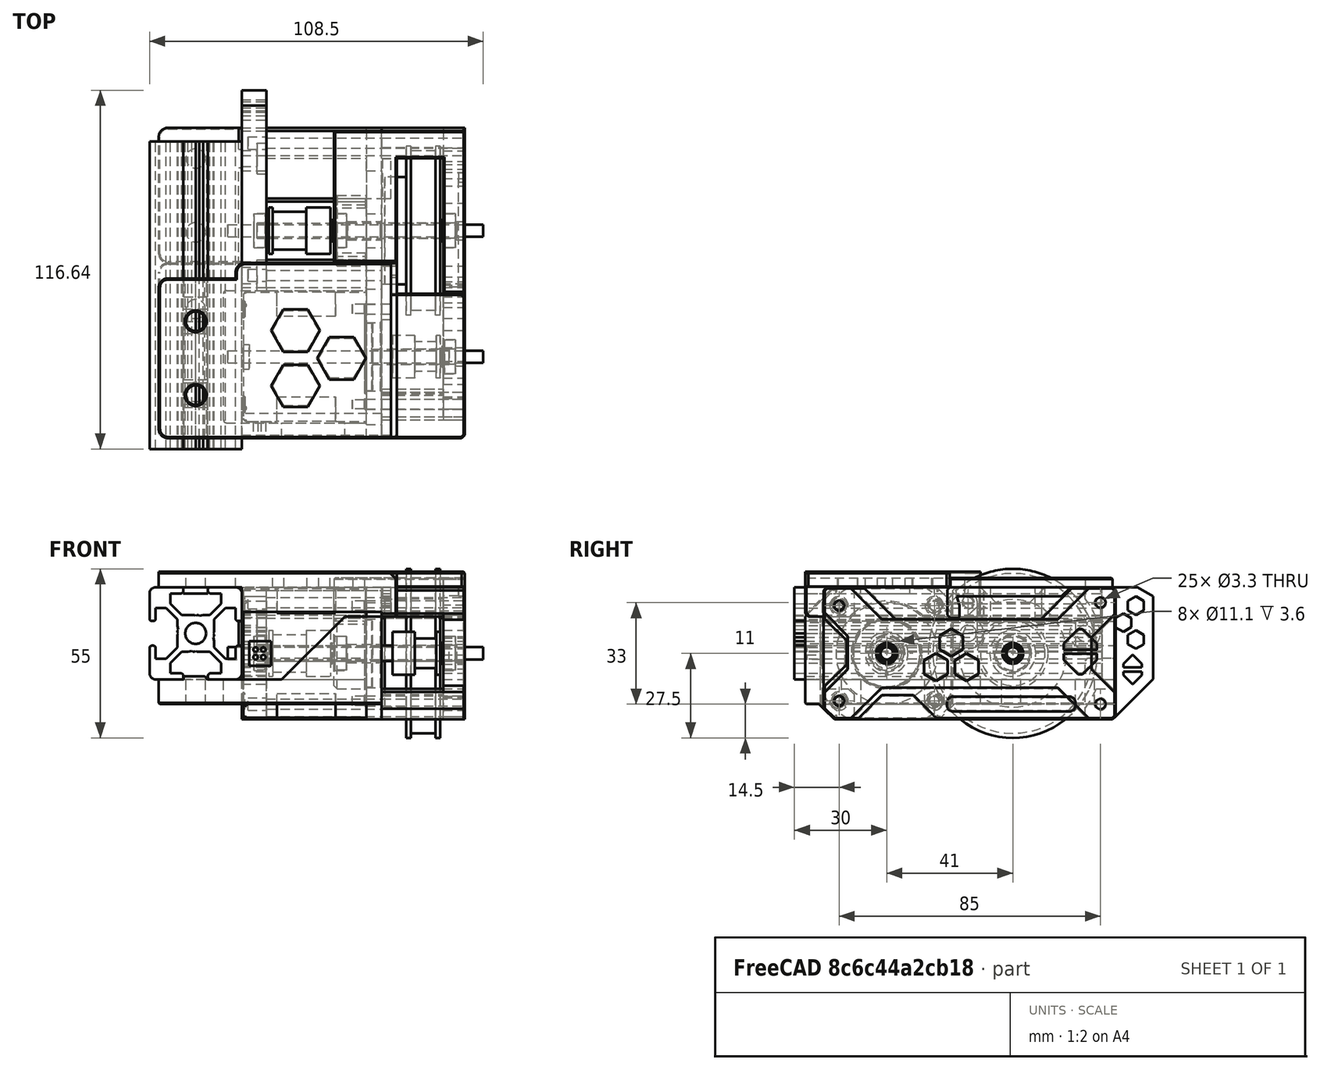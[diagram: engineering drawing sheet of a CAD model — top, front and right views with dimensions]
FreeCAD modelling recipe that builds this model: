
FCSTD DOCUMENT  (FreeCAD 0.19R24291 (Git))
Label: 80t-gearbox-old
License: Other
LicenseURL: GPL3
objects: Part::Cylinder×41, Part::Box×39, Part::Chamfer×38, Part::Cut×30, Part::MultiFuse×30, Part::Feature×29, Part::Fillet×4, Part::Refine×3
note: 214 computed .brp shape members not serialized (recipe doc carries the construction recipe); baked Part::Feature solids carry a one-line shape summary decoded from their .brp

FEATURE [Part::Feature] Cut001002  label="80t-pulley"
  Placement = pos=(64.5,41,8.5) rot=(0.707107,0,-0.707107;3.14159rad)
  shape: bbox 18 x 55 x 55 mm, 10 faces (baked)
FEATURE [Part::Feature] Cut001001  label="16t-pulley"
  Placement = pos=(64.5,0,8.5) rot=(0,-1,0;1.5708rad)
  shape: bbox 15.5 x 13.9 x 13.9 mm, 8 faces (baked)
FEATURE [Part::Feature] Fusion006002011004053036004001001  label="motor-40mm"
  Placement = pos=(0.5,0,8.5) rot=(0,1,0;1.5708rad)
  shape: bbox 67 x 47 x 42 mm, 100 faces (baked)
FEATURE [Part::Feature] Extrude001003002002002002  label="Extrude001003002002004"
  Placement = pos=(-15,-30,15) rot=(-1,0,0;1.5708rad)
  shape: bbox 30 x 100 x 30 mm, 95 faces (baked)
FEATURE [Part::Feature] Cut001  label="20t-pulley"
  Placement = pos=(8.8,41,8.5) rot=(0.707107,0,0.707107;3.14159rad)
  shape: bbox 20 x 15 x 15 mm, 8 faces (baked)
FEATURE [Part::Feature] Cut001003  label="MR115ZZ001"
  Placement = pos=(69.5,0,8.5) rot=(0,-1,0;1.5708rad)
  shape: bbox 4 x 11 x 11 mm, 4 faces (baked)
FEATURE [Part::Feature] Cut001004  label="MR115ZZ002"
  Placement = pos=(69.5,41,8.5) rot=(0,-1,0;1.5708rad)
  shape: bbox 4 x 11 x 11 mm, 4 faces (baked)
FEATURE [Part::Feature] Cut001005  label="MR115ZZ003"
  Placement = pos=(34,41,8.5) rot=(0,-1,0;1.5708rad)
  shape: bbox 4 x 11 x 11 mm, 4 faces (baked)
FEATURE [Part::Cylinder] Cylinder  label="POSA"
  Angle = 360
  AttacherType = Attacher::AttachEngine3D
  Height = 83
  Placement = pos=(-4.5,0,8.5) rot=(0,1,0;1.5708rad)
  Radius = 2
FEATURE [Part::Cylinder] Cylinder001  label="POSB"
  Angle = 360
  AttacherType = Attacher::AttachEngine3D
  Height = 83
  Placement = pos=(-4.5,41,8.5) rot=(0,1,0;1.5708rad)
  Radius = 2
FEATURE [Part::Box] Box  label="Cube"
  AttacherType = Attacher::AttachEngine3D
  Height = 43
  Length = 5
  Placement = pos=(40.5,-26.5,-13) rot=(0,0,1;0rad)
  Width = 101
FEATURE [Part::Box] Box001  label="Cube001"
  AttacherType = Attacher::AttachEngine3D
  Height = 43
  Length = 8
  Placement = pos=(0,21.5,-13) rot=(0,0,1;0rad)
  Width = 53
FEATURE [Part::Cylinder] Cylinder002  label="br01"
  Angle = 360
  AttacherType = Attacher::AttachEngine3D
  Height = 4
  Placement = pos=(4,41,8.5) rot=(0,1,0;1.5708rad)
  Radius = 5.55
FEATURE [Part::Cylinder] Cylinder003  label="br002"
  Angle = 360
  AttacherType = Attacher::AttachEngine3D
  Height = 4
  Placement = pos=(30,41,8.5) rot=(0,1,0;1.5708rad)
  Radius = 5.55
FEATURE [Part::Cylinder] Cylinder004  label="br003"
  Angle = 360
  AttacherType = Attacher::AttachEngine3D
  Height = 4
  Placement = pos=(65.5,41,8.5) rot=(0,1,0;1.5708rad)
  Radius = 5.55
FEATURE [Part::Cylinder] Cylinder005  label="br004"
  Angle = 360
  AttacherType = Attacher::AttachEngine3D
  Height = 4
  Placement = pos=(65.5,0,8.5) rot=(0,1,0;1.5708rad)
  Radius = 5.55
FEATURE [Part::Box] Box002  label="Cube002"
  AttacherType = Attacher::AttachEngine3D
  Height = 8
  Length = 27
  Placement = pos=(-27,30.5,-8) rot=(0,0,1;0rad)
  Width = 44
FEATURE [Part::Box] Box003  label="Cube003"
  AttacherType = Attacher::AttachEngine3D
  Height = 7.8
  Length = 1
  Placement = pos=(-1,29.5,11.1) rot=(0,0,1;0rad)
  Width = 32
FEATURE [Part::Feature] Cut001006  label="MR115ZZ004"
  Placement = pos=(8,41,8.5) rot=(0,-1,0;1.5708rad)
  shape: bbox 4 x 11 x 11 mm, 4 faces (baked)
FEATURE [Part::Cut] Cut
  Base = -> Box001
  Tool = -> Cylinder002
FEATURE [Part::Chamfer] Chamfer
  Base = -> Cut
  Edges = 1 edges r=0.4: [Edge13]
FEATURE [Part::Cylinder] Cylinder006  label="Cylinder"
  Angle = 360
  AttacherType = Attacher::AttachEngine3D
  Height = 10
  Placement = pos=(-3e-15,26.5,15) rot=(0,1,0;1.5708rad)
  Radius = 2.65
FEATURE [Part::Cylinder] Cylinder007  label="Cylinder001"
  Angle = 360
  AttacherType = Attacher::AttachEngine3D
  Height = 3
  Placement = pos=(5,26.5,15) rot=(0,1,0;1.5708rad)
  Radius = 5
FEATURE [Part::MultiFuse] Fusion
  Shapes = -> [Cylinder007,Cylinder006]
FEATURE [Part::Feature] Fusion006002011004053036004001002  label="Fusion001"
  Placement = pos=(0,38,0) rot=(0,0,1;0rad)
  shape: bbox 10 x 10 x 10 mm, 7 faces (baked)
FEATURE [Part::MultiFuse] Fusion006002011004053036004001003
  Shapes = -> [Fusion,Fusion006002011004053036004001002]
FEATURE [Part::Box] Box004  label="Cube004"
  AttacherType = Attacher::AttachEngine3D
  Height = 10
  Length = 3
  Placement = pos=(5,16.5,10) rot=(0,0,1;0rad)
  Width = 10
FEATURE [Part::MultiFuse] Fusion006002011004053036004001004
  Shapes = -> [Box004,Fusion006002011004053036004001003]
FEATURE [Part::Cut] Cut001007
  Base = -> Chamfer
  Tool = -> Fusion006002011004053036004001004
FEATURE [Part::Box] Box005  label="Cube005"
  AttacherType = Attacher::AttachEngine3D
  Height = 7.8
  Length = 1
  Placement = pos=(-1,67.5,11.1) rot=(0,0,1;0rad)
  Width = 7
FEATURE [Part::Box] Box006  label="Cube006"
  AttacherType = Attacher::AttachEngine3D
  Height = 13
  Length = 10
  Placement = pos=(-1.5,20.5,-13) rot=(0,0,1;0rad)
  Width = 10
FEATURE [Part::Cut] Cut001008
  Base = -> Cut001007
  Tool = -> Box006
FEATURE [Part::Chamfer] Chamfer001
  Base = -> Cut001008
  Edges = 1 edges r=5: [Edge30]
FEATURE [Part::Fillet] Fillet
  Base = -> Box002
  Edges = 2 edges r=3: [Edge1,Edge3]
FEATURE [Part::Box] Box007  label="Cube007"
  AttacherType = Attacher::AttachEngine3D
  Height = 28.5
  Length = 28
  Placement = pos=(13,-26.5,-8) rot=(0,0,1;0rad)
  Width = 5
FEATURE [Part::Box] Box009  label="Cube009"
  AttacherType = Attacher::AttachEngine3D
  Height = 8
  Length = 72
  Placement = pos=(-27,-26.5,-8) rot=(0,0,1;0rad)
  Width = 57
FEATURE [Part::Box] Box010  label="Cube010"
  AttacherType = Attacher::AttachEngine3D
  Height = 8
  Length = 40.5
  Placement = pos=(0,-21.5,-8) rot=(0,0,1;0rad)
  Width = 43
FEATURE [Part::Fillet] Fillet001
  Base = -> Box009
  Edges = 2 edges r=3: [Edge1,Edge3]
FEATURE [Part::Cut] Cut001009
  Base = -> Fillet001
  Tool = -> Box010
FEATURE [Part::Box] Box011  label="Cube011"
  AttacherType = Attacher::AttachEngine3D
  Height = 10
  Length = 33
  Placement = pos=(8,50.5,20) rot=(0,0,1;0rad)
  Width = 24
FEATURE [Part::Box] Box012  label="Cube012"
  AttacherType = Attacher::AttachEngine3D
  Height = 20
  Length = 33
  Placement = pos=(8,64.5,-13) rot=(0,0,1;0rad)
  Width = 10
FEATURE [Part::Box] Box013  label="Cube013"
  AttacherType = Attacher::AttachEngine3D
  Height = 10
  Length = 33
  Placement = pos=(8,21.5,20) rot=(0,0,1;0rad)
  Width = 10
FEATURE [Part::Chamfer] Chamfer002
  Base = -> Chamfer001
  Edges = 4 edges r=1: [Edge16,Edge19,Edge24,Edge25]
FEATURE [Part::Chamfer] Chamfer005
  Base = -> Box013
  Edges = 4 edges r=1: [Edge9,Edge10,Edge11,Edge12]
FEATURE [Part::Chamfer] Chamfer006
  Base = -> Chamfer002
  Edges = 2 edges r=1: [Edge39,Edge43]
FEATURE [Part::Box] Box014  label="Cube014"
  AttacherType = Attacher::AttachEngine3D
  Height = 10
  Length = 10
  Placement = pos=(-1,30.5,-18) rot=(0,0,1;0rad)
  Width = 35
FEATURE [Part::Chamfer] Chamfer007
  Base = -> Box014
  Edges = 1 edges r=5: [Edge12]
FEATURE [Part::Cut] Cut001010
  Base = -> Chamfer006
  Tool = -> Chamfer007
FEATURE [Part::Cylinder] Cylinder008  label="Cylinder002"
  Angle = 360
  AttacherType = Attacher::AttachEngine3D
  Height = 110
  Placement = pos=(2,26.5,25) rot=(0,1,0;1.5708rad)
  Radius = 1.65
FEATURE [Part::Cylinder] Cylinder009  label="Cylinder003"
  Angle = 360
  AttacherType = Attacher::AttachEngine3D
  Height = 110
  Placement = pos=(2,69.5,25) rot=(0,1,0;1.5708rad)
  Radius = 1.65
FEATURE [Part::Cylinder] Cylinder010  label="Cylinder004"
  Angle = 360
  AttacherType = Attacher::AttachEngine3D
  Height = 110
  Placement = pos=(2,69.5,-8) rot=(0,1,0;1.5708rad)
  Radius = 1.65
FEATURE [Part::Cylinder] Cylinder011  label="Cylinder005"
  Angle = 360
  AttacherType = Attacher::AttachEngine3D
  Height = 6
  Placement = pos=(2,69.5,-8) rot=(0,1,0;1.5708rad)
  Radius = 2
FEATURE [Part::Cylinder] Cylinder012  label="Cylinder006"
  Angle = 360
  AttacherType = Attacher::AttachEngine3D
  Height = 6
  Placement = pos=(2,69.5,25) rot=(0,1,0;1.5708rad)
  Radius = 2
FEATURE [Part::Cylinder] Cylinder013  label="Cylinder007"
  Angle = 360
  AttacherType = Attacher::AttachEngine3D
  Height = 6
  Placement = pos=(2,26.5,25) rot=(0,1,0;1.5708rad)
  Radius = 2
FEATURE [Part::MultiFuse] Fusion006002011004053036004001006
  Shapes = -> [Cylinder013,Cylinder012,Cylinder011]
FEATURE [Part::Cut] Cut001011
  Base = -> Cut001010
  Tool = -> Fusion006002011004053036004001006
FEATURE [Part::MultiFuse] Fusion006002011004053036004001007
  Shapes = -> [Cylinder010,Cylinder008,Cylinder009]
FEATURE [Part::Chamfer] Chamfer008
  Base = -> Box
  Edges = 2 edges r=1: [Edge11,Edge12]
FEATURE [Part::Chamfer] Chamfer009
  Base = -> Box011
  Edges = 4 edges r=1: [Edge9,Edge10,Edge11,Edge12]
FEATURE [Part::Cylinder] Cylinder014  label="Cylinder008"
  Angle = 360
  AttacherType = Attacher::AttachEngine3D
  Height = 10
  Placement = pos=(-15,40.5,0) rot=(0,0,1;0rad)
  Radius = 3.15
FEATURE [Part::Cylinder] Cylinder015  label="Cylinder009"
  Angle = 360
  AttacherType = Attacher::AttachEngine3D
  Height = 10
  Placement = pos=(-15,64.5,0) rot=(0,0,1;0rad)
  Radius = 3.15
FEATURE [Part::MultiFuse] Fusion006002011004053036004001009
  Placement = pos=(0,0,-10) rot=(0,0,1;0rad)
  Shapes = -> [Cylinder014,Cylinder015]
FEATURE [Part::Cut] Cut001012
  Base = -> Fillet
  Tool = -> Fusion006002011004053036004001009
FEATURE [Part::Chamfer] Chamfer011
  Base = -> Cut001012
  Edges = 5 edges r=0.4: [Edge4,Edge12,Edge14,Edge16,Edge17]
FEATURE [Part::Chamfer] Chamfer012
  Base = -> Cut001011
  Edges = 1 edges r=0.4: [Edge45]
FEATURE [Part::MultiFuse] Fusion006002011004053036004001010
  Shapes = -> [Box005,Box003]
FEATURE [Part::MultiFuse] Fusion006002011004053036004001011  label="back-plate"
  Shapes = -> [Chamfer012,Fusion006002011004053036004001010,Chamfer011]
FEATURE [Part::Box] Box015  label="Cube015"
  AttacherType = Attacher::AttachEngine3D
  Height = 10
  Length = 10
  Placement = pos=(36.5,17,-18) rot=(0,0,1;0rad)
  Width = 48.5
FEATURE [Part::Box] Box016  label="Cube016"
  AttacherType = Attacher::AttachEngine3D
  Height = 10
  Length = 10
  Placement = pos=(36.5,-75.5,-18) rot=(0,0,1;0rad)
  Width = 58.5
FEATURE [Part::Chamfer] Chamfer013
  Base = -> Box016
  Edges = 1 edges r=5: [Edge12]
FEATURE [Part::Cut] Cut001013
  Base = -> Chamfer008
  Tool = -> Chamfer013
FEATURE [Part::Chamfer] Chamfer014
  Base = -> Box015
  Edges = 2 edges r=5: [Edge10,Edge12]
FEATURE [Part::Cut] Cut001014
  Base = -> Cut001013
  Tool = -> Chamfer014
FEATURE [Part::Chamfer] Chamfer015
  Base = -> Cut001014
  Edges = 1 edges r=9.5: [Edge33]
FEATURE [Part::Chamfer] Chamfer016
  Base = -> Cut001009
  Edges = 5 edges r=0.4: [Edge4,Edge14,Edge16,Edge18,Edge19]
FEATURE [Part::Cylinder] Cylinder016  label="POSA001"
  Angle = 360
  AttacherType = Attacher::AttachEngine3D
  Height = 83
  Placement = pos=(2.5,0,8.5) rot=(0,1,0;1.5708rad)
  Radius = 11.15
FEATURE [Part::Chamfer] Chamfer017
  Base = -> Chamfer015
  Edges = 1 edges r=0.4: [Edge16]
FEATURE [Part::Cylinder] Cylinder017  label="Cylinder010"
  Angle = 360
  AttacherType = Attacher::AttachEngine3D
  Height = 10
  Placement = pos=(-15,15.5,0) rot=(0,0,1;0rad)
  Radius = 3.15
FEATURE [Part::Cylinder] Cylinder018  label="Cylinder011"
  Angle = 360
  AttacherType = Attacher::AttachEngine3D
  Height = 10
  Placement = pos=(-15,-11.5,0) rot=(0,0,1;0rad)
  Radius = 3.15
FEATURE [Part::MultiFuse] Fusion006002011004053036004001012
  Placement = pos=(0,0,-9) rot=(0,0,1;0rad)
  Shapes = -> [Cylinder017,Cylinder018]
FEATURE [Part::Cut] Cut001015
  Base = -> Chamfer016
  Tool = -> Fusion006002011004053036004001012
FEATURE [Part::Chamfer] Chamfer018
  Base = -> Box007
  Edges = 1 edges r=0.5: [Edge9]
FEATURE [Part::Chamfer] Chamfer019
  Base = -> Chamfer018
  Edges = 1 edges r=20.5: [Edge3]
FEATURE [Part::Box] Box017  label="Cube017"
  AttacherType = Attacher::AttachEngine3D
  Height = 2
  Length = 7.8
  Placement = pos=(-18.9,-26.5,0) rot=(0,0,1;0rad)
  Width = 11
FEATURE [Part::Box] Box018  label="Cube018"
  AttacherType = Attacher::AttachEngine3D
  Height = 2
  Length = 7.8
  Placement = pos=(-18.9,-7.5,0) rot=(0,0,1;0rad)
  Width = 19
FEATURE [Part::Box] Box019  label="Cube019"
  AttacherType = Attacher::AttachEngine3D
  Height = 2
  Length = 7.8
  Placement = pos=(-18.9,19.5,0) rot=(0,0,1;0rad)
  Width = 11
FEATURE [Part::MultiFuse] Fusion006002011004053036004001013
  Placement = pos=(0,0,-1) rot=(0,0,1;0rad)
  Shapes = -> [Box018,Box019,Box017]
FEATURE [Part::Chamfer] Chamfer020
  Base = -> Fusion006002011004053036004001013
  Edges = 3 edges r=1: [Edge6,Edge18,Edge30]
FEATURE [Part::MultiFuse] Fusion006002011004053036004001014
  Shapes = -> [Chamfer020,Cut001015]
FEATURE [Part::MultiFuse] Fusion006002011004053036004001015
  Shapes = -> [Fusion006002011004053036004001014,Chamfer019,Chamfer017]
FEATURE [Part::Cut] Cut001016
  Base = -> Fusion006002011004053036004001015
  Tool = -> Cylinder016
FEATURE [Part::Cylinder] Cylinder019  label="POSA002"
  Angle = 360
  AttacherType = Attacher::AttachEngine3D
  Height = 30
  Placement = pos=(32,15.5,24) rot=(0,1,0;1.5708rad)
  Radius = 1.65
FEATURE [Part::Cylinder] Cylinder020  label="POSA003"
  Angle = 360
  AttacherType = Attacher::AttachEngine3D
  Height = 30
  Placement = pos=(32,-15.5,24) rot=(0,1,0;1.5708rad)
  Radius = 1.65
FEATURE [Part::Cylinder] Cylinder021  label="POSA004"
  Angle = 360
  AttacherType = Attacher::AttachEngine3D
  Height = 30
  Placement = pos=(32,-15.5,-7) rot=(0,1,0;1.5708rad)
  Radius = 1.65
FEATURE [Part::Cylinder] Cylinder022  label="POSA005"
  Angle = 360
  AttacherType = Attacher::AttachEngine3D
  Height = 30
  Placement = pos=(32,15.5,-7) rot=(0,1,0;1.5708rad)
  Radius = 1.65
FEATURE [Part::MultiFuse] Fusion006002011004053036004001016
  Shapes = -> [Cylinder022,Cylinder021,Cylinder020,Cylinder019]
FEATURE [Part::Cut] Cut001017
  Base = -> Cut001016
  Tool = -> Fusion006002011004053036004001016
FEATURE [Part::Cylinder] Cylinder023  label="POSB001"
  Angle = 360
  AttacherType = Attacher::AttachEngine3D
  Height = 12
  Placement = pos=(30,41,8.5) rot=(0,1,0;1.5708rad)
  Radius = 11.5
FEATURE [Part::Chamfer] Chamfer021
  Base = -> Cylinder023
  Edges = 1 edges r=1: [Edge3]
FEATURE [Part::Cut] Cut001018
  Base = -> Chamfer021
  Tool = -> Cylinder003
FEATURE [Part::Chamfer] Chamfer022
  Base = -> Cut001018
  Edges = 1 edges r=0.4: [Edge6]
FEATURE [Part::Cylinder] Cylinder024  label="POSB002"
  Angle = 360
  AttacherType = Attacher::AttachEngine3D
  Height = 83
  Placement = pos=(-4.5,41,8.5) rot=(0,1,0;1.5708rad)
  Radius = 3
FEATURE [Part::Chamfer] Chamfer023
  Base = -> Box012
  Edges = 4 edges r=1: [Edge9,Edge10,Edge11,Edge12]
FEATURE [Part::MultiFuse] Fusion006002011004053036004001017
  Shapes = -> [Chamfer023,Chamfer009,Chamfer005]
FEATURE [Part::MultiFuse] Fusion006002011004053036004001018
  Shapes = -> [Cut001017,Chamfer022]
FEATURE [Part::Cut] Cut001019
  Base = -> Fusion006002011004053036004001018
  Tool = -> Cylinder024
FEATURE [Part::Chamfer] Chamfer024
  Base = -> Cut001019
  Edges = 3 edges r=0.4: [Edge126,Edge173,Edge202]
FEATURE [Part::MultiFuse] Fusion006002011004053036004001019
  Shapes = -> [Chamfer024,Fusion006002011004053036004001017]
FEATURE [Part::Box] Box020  label="Cube020"
  AttacherType = Attacher::AttachEngine3D
  Height = 10
  Length = 10
  Placement = pos=(38.5,30.5,35) rot=(0,0,1;0rad)
  Width = 21
FEATURE [Part::Chamfer] Chamfer025
  Base = -> Box020
  Edges = 2 edges r=5: [Edge9,Edge11]
  Placement = pos=(0,0,-10) rot=(0,0,1;0rad)
FEATURE [Part::Cut] Cut001020
  Base = -> Fusion006002011004053036004001019
  Tool = -> Fusion006002011004053036004001007
FEATURE [Part::Cut] Cut001021  label="z-motor-plate"
  Base = -> Cut001020
  Tool = -> Chamfer025
FEATURE [Part::Box] Box021  label="Cube021"
  AttacherType = Attacher::AttachEngine3D
  Height = 10
  Length = 5
  Placement = pos=(45.5,-26.5,20.5) rot=(0,0,1;0rad)
  Width = 57
FEATURE [Part::Box] Box022  label="Cube022"
  AttacherType = Attacher::AttachEngine3D
  Height = 9
  Length = 50.5
  Placement = pos=(0,-26.5,22) rot=(0,0,1;0rad)
  Width = 8
FEATURE [Part::Chamfer] Chamfer026
  Base = -> Box022
  Edges = 1 edges r=7: [Edge11]
FEATURE [Part::Box] Box023  label="Cube023"
  AttacherType = Attacher::AttachEngine3D
  Height = 5
  Length = 77.5
  Placement = pos=(-27,-26.5,30) rot=(0,0,1;0rad)
  Width = 57
FEATURE [Part::Chamfer] Chamfer027
  Base = -> Box021
  Edges = 2 edges r=1: [Edge9,Edge11]
FEATURE [Part::Cylinder] Cylinder025  label="POSA006"
  Angle = 360
  AttacherType = Attacher::AttachEngine3D
  Height = 83
  Placement = pos=(18.5,0,8.5) rot=(0,1,0;1.5708rad)
  Radius = 17
FEATURE [Part::Cut] Cut001022
  Base = -> Chamfer027
  Tool = -> Cylinder025
FEATURE [Part::Box] Box024  label="Cube024"
  AttacherType = Attacher::AttachEngine3D
  Height = 2
  Length = 8
  Placement = pos=(-19,-8.5,28) rot=(0,0,1;0rad)
  Width = 16
FEATURE [Part::Box] Box025  label="Cube025"
  AttacherType = Attacher::AttachEngine3D
  Height = 2
  Length = 8
  Placement = pos=(-19,-26.5,28) rot=(0,0,1;0rad)
  Width = 10
FEATURE [Part::Box] Box026  label="Cube026"
  AttacherType = Attacher::AttachEngine3D
  Height = 2
  Length = 8
  Placement = pos=(-19,15.5,28) rot=(0,0,1;0rad)
  Width = 10
FEATURE [Part::Cylinder] Cylinder026  label="Cylinder012"
  Angle = 360
  AttacherType = Attacher::AttachEngine3D
  Height = 10
  Placement = pos=(-15,11.5,26) rot=(0,0,1;0rad)
  Radius = 3.15
FEATURE [Part::Cylinder] Cylinder027  label="Cylinder013"
  Angle = 360
  AttacherType = Attacher::AttachEngine3D
  Height = 10
  Placement = pos=(-15,-12.5,26) rot=(0,0,1;0rad)
  Radius = 3.15
FEATURE [Part::Cylinder] Cylinder028  label="POSA007"
  Angle = 360
  AttacherType = Attacher::AttachEngine3D
  Height = 83
  Placement = pos=(25.5,-15.5,24) rot=(0,1,0;1.5708rad)
  Radius = 1.65
FEATURE [Part::Cylinder] Cylinder029  label="POSA008"
  Angle = 360
  AttacherType = Attacher::AttachEngine3D
  Height = 83
  Placement = pos=(25.5,15.5,24) rot=(0,1,0;1.5708rad)
  Radius = 1.65
FEATURE [Part::MultiFuse] Fusion006002011004053036004001024
  Shapes = -> [Cylinder029,Cylinder028]
FEATURE [Part::Box] Box027  label="Cube027"
  AttacherType = Attacher::AttachEngine3D
  Height = 10
  Length = 26
  Placement = pos=(45.5,64.5,-13) rot=(0,0,1;0rad)
  Width = 10
FEATURE [Part::Box] Box028  label="Cube028"
  AttacherType = Attacher::AttachEngine3D
  Height = 10
  Length = 26
  Placement = pos=(45.5,64.5,20) rot=(0,0,1;0rad)
  Width = 10
FEATURE [Part::Box] Box029  label="Cube029"
  AttacherType = Attacher::AttachEngine3D
  Height = 9.5
  Length = 21
  Placement = pos=(50.5,-20.5,20.5) rot=(0,0,1;0rad)
  Width = 10
FEATURE [Part::Box] Box030  label="Cube030"
  AttacherType = Attacher::AttachEngine3D
  Height = 10
  Length = 26
  Placement = pos=(45.5,-20.5,-13) rot=(0,0,1;0rad)
  Width = 10
FEATURE [Part::Cylinder] Cylinder030  label="POSB003"
  Angle = 360
  AttacherType = Attacher::AttachEngine3D
  Height = 83
  Placement = pos=(20.5,41,8.5) rot=(0,1,0;1.5708rad)
  Radius = 29.5
FEATURE [Part::Cylinder] Cylinder031  label="POSA009"
  Angle = 360
  AttacherType = Attacher::AttachEngine3D
  Height = 83
  Placement = pos=(-4.5,0,8.5) rot=(0,1,0;1.5708rad)
  Radius = 17
FEATURE [Part::MultiFuse] Fusion006002011004053036004001025
  Shapes = -> [Box030,Box029,Box027,Box028]
FEATURE [Part::Cut] Cut001024002
  Base = -> Fusion006002011004053036004001025
  Tool = -> Cylinder030
FEATURE [Part::Chamfer] Chamfer030
  Base = -> Cut001024002
  Edges = 1 edges r=3.5: [Edge9]
FEATURE [Part::Cut] Cut001024003
  Base = -> Chamfer030
  Tool = -> Cylinder031
FEATURE [Part::Chamfer] Chamfer031
  Base = -> Cut001024003
  Edges = 11 edges r=1: [Edge9,Edge15,Edge24,Edge26,Edge32,Edge41,Edge44,Edge46,Edge55,Edge57,Edge59]
FEATURE [Part::Box] Box032  label="Cube032"
  AttacherType = Attacher::AttachEngine3D
  Height = 43
  Length = 7
  Placement = pos=(65.5,-20.5,-13) rot=(0,0,1;0rad)
  Width = 95
FEATURE [Part::Chamfer] Chamfer032
  Base = -> Box032
  Edges = 1 edges r=3.5: [Edge9]
FEATURE [Part::Chamfer] Chamfer033
  Base = -> Chamfer032
  Edges = 3 edges r=1: [Edge8,Edge11,Edge13]
FEATURE [Part::Cylinder] Cylinder032  label="POSB004"
  Angle = 360
  AttacherType = Attacher::AttachEngine3D
  Height = 83
  Placement = pos=(-4.5,41,8.5) rot=(0,1,0;1.5708rad)
  Radius = 3
FEATURE [Part::Cylinder] Cylinder033  label="POSA010"
  Angle = 360
  AttacherType = Attacher::AttachEngine3D
  Height = 83
  Placement = pos=(-4.5,0,8.5) rot=(0,1,0;1.5708rad)
  Radius = 3
FEATURE [Part::MultiFuse] Fusion006002011004053036004001026
  Shapes = -> [Cylinder033,Cylinder032,Cylinder005,Cylinder004]
FEATURE [Part::Cut] Cut001024004
  Base = -> Chamfer033
  Tool = -> Fusion006002011004053036004001026
FEATURE [Part::Chamfer] Chamfer034
  Base = -> Cut001024004
  Edges = 4 edges r=0.4: [Edge9,Edge10,Edge31,Edge32]
FEATURE [Part::Feature] Fusion006002011004053036004001028001  label="dog-bone-plate"
  shape: bbox 27 x 95 x 43 mm, 76 faces (baked)
FEATURE [Part::Cylinder] Cylinder034  label="POSB005"
  Angle = 360
  AttacherType = Attacher::AttachEngine3D
  Height = 83
  Placement = pos=(-4.5,69.5,-8) rot=(0,1,0;1.5708rad)
  Radius = 1.65
FEATURE [Part::Cylinder] Cylinder035  label="POSA011"
  Angle = 360
  AttacherType = Attacher::AttachEngine3D
  Height = 83
  Placement = pos=(-4.5,-15.5,-7) rot=(0,1,0;1.5708rad)
  Radius = 1.65
FEATURE [Part::Cylinder] Cylinder036  label="POSB006"
  Angle = 360
  AttacherType = Attacher::AttachEngine3D
  Height = 83
  Placement = pos=(-4.5,69.5,25) rot=(0,1,0;1.5708rad)
  Radius = 1.65
FEATURE [Part::Cylinder] Cylinder037  label="POSA012"
  Angle = 360
  AttacherType = Attacher::AttachEngine3D
  Height = 83
  Placement = pos=(-4.5,-15.5,24) rot=(0,1,0;1.5708rad)
  Radius = 1.65
FEATURE [Part::MultiFuse] Fusion006002011004053036004001028003
  Shapes = -> [Cylinder037,Cylinder036,Cylinder035,Cylinder034]
FEATURE [Part::Cut] Cut001024005  label="dog-bone-plate-r1"
  Base = -> Fusion006002011004053036004001028001
  Tool = -> Fusion006002011004053036004001028003
FEATURE [Part::Feature] Fusion006002011004053036004001028003001  label="Fusion006002011004053036004001028004"
  shape: bbox 83 x 88.3 x 36.3 mm, 12 faces, 4 solids (baked)
FEATURE [Part::MultiFuse] Fusion006002011004053036004001028003002
  Shapes = -> [Chamfer034,Chamfer031]
FEATURE [Part::Cut] Cut001024006  label="face-plate-plain"
  Base = -> Fusion006002011004053036004001028003002
  Tool = -> Fusion006002011004053036004001028003001
FEATURE [Part::Feature] Cut001024007  label="5mm-washer001"
  Placement = pos=(65,0,8.5) rot=(0,1,0;1.5708rad)
  shape: bbox 0.5 x 6.9 x 6.9 mm, 4 faces (baked)
FEATURE [Part::Feature] Cut001024008  label="5mm-washer002"
  Placement = pos=(65,41,8.5) rot=(0,1,0;1.5708rad)
  shape: bbox 0.5 x 6.9 x 6.9 mm, 4 faces (baked)
FEATURE [Part::Feature] Cut001024009  label="5mm-washer003"
  Placement = pos=(8,41,8.5) rot=(0,1,0;1.5708rad)
  shape: bbox 0.5 x 6.9 x 6.9 mm, 4 faces (baked)
FEATURE [Part::Feature] Cut001024010  label="5mm-washer004"
  Placement = pos=(29,41,8.5) rot=(0,1,0;1.5708rad)
  shape: bbox 0.5 x 6.9 x 6.9 mm, 4 faces (baked)
FEATURE [Part::Box] Box033  label="Cube033"
  AttacherType = Attacher::AttachEngine3D
  Height = 43
  Length = 8
  Placement = pos=(0,72.5,-13) rot=(0,0,1;0rad)
  Width = 14.14
FEATURE [Part::Feature] Body001  label="hex-cut"
  Placement = pos=(-5e-15,81,24) rot=(0,1,0;1.5708rad)
  shape: bbox 10 x 5.196 x 6 mm, 8 faces (baked)
FEATURE [Part::Feature] Body002  label="hex-cut001"
  Placement = pos=(-3.8e-15,77,18.5) rot=(0,1,0;1.5708rad)
  shape: bbox 10 x 5.196 x 6 mm, 8 faces (baked)
FEATURE [Part::Feature] Body004  label="hex-cut003"
  Placement = pos=(-3e-15,81,13) rot=(0,1,0;1.5708rad)
  shape: bbox 10 x 5.196 x 6 mm, 8 faces (baked)
FEATURE [Part::Chamfer] Chamfer035
  Base = -> Box033
  Edges = 1 edges: [Edge12 r1=3 r2=5]
FEATURE [Part::Chamfer] Chamfer036
  Base = -> Chamfer035
  Edges = 1 edges r=13.14: [Edge14]
FEATURE [Part::Box] Box034  label="Cube034"
  AttacherType = Attacher::AttachEngine3D
  Height = 4
  Length = 10
  Placement = pos=(0,77,4) rot=(0,0,1;0rad)
  Width = 6
FEATURE [Part::Box] Box035  label="Cube035"
  AttacherType = Attacher::AttachEngine3D
  Height = 4
  Length = 10
  Placement = pos=(0,77,-1.5) rot=(0,0,1;0rad)
  Width = 6
FEATURE [Part::MultiFuse] Fusion006002011004053036004001028003003
  Shapes = -> [Box035,Box034]
FEATURE [Part::Chamfer] Chamfer037
  Base = -> Fusion006002011004053036004001028003003
  Edges = 4 edges r=2.9: [Edge9,Edge11,Edge22,Edge24]
FEATURE [Part::MultiFuse] Fusion006002011004053036004001028003004
  Shapes = -> [Chamfer037,Body004,Body002,Body001]
FEATURE [Part::Cut] Cut001024011
  Base = -> Chamfer036
  Tool = -> Fusion006002011004053036004001028003004
FEATURE [Part::MultiFuse] Fusion006002011004053036004001028003005  label="back-plate-w-aligner"
  Shapes = -> [Fusion006002011004053036004001011,Cut001024011]
FEATURE [Part::Cylinder] Cylinder038  label="5x65-shaft"
  Angle = 360
  AttacherType = Attacher::AttachEngine3D
  Height = 65
  Placement = pos=(5,41,8.5) rot=(0,1,0;1.5708rad)
  Radius = 2.5
FEATURE [Part::Feature] Chamfer029006001  label="front-plate-type001"
  Placement = pos=(65.5,-1.5e-14,1e-15) rot=(0.57735,0.57735,0.57735;2.0944rad)
  shape: bbox 27 x 95 x 43 mm, 156 faces (baked)
FEATURE [Part::Box] Box036  label="Cube036"
  AttacherType = Attacher::AttachEngine3D
  Height = 10
  Length = 28
  Placement = pos=(-30,25.5,25) rot=(0,0,1;0rad)
  Width = 14
FEATURE [Part::Cut] Cut001024012
  Base = -> Box023
  Tool = -> Box036
FEATURE [Part::Fillet] Fillet002
  Base = -> Cut001024012
  Edges = 3 edges r=3: [Edge2,Edge4,Edge17]
FEATURE [Part::MultiFuse] Fusion006002011004053036004001028003006
  Shapes = -> [Box026,Box025]
FEATURE [Part::MultiFuse] Fusion006002011004053036004001028003007
  Shapes = -> [Fillet002,Chamfer026,Cut001022,Box024]
FEATURE [Part::Cut] Cut001024013
  Base = -> Fusion006002011004053036004001028003007
  Tool = -> Fusion006002011004053036004001024
FEATURE [Part::MultiFuse] Fusion006002011004053036004001028003008
  Shapes = -> [Cylinder027,Cylinder026]
FEATURE [Part::Cut] Cut001024014
  Base = -> Cut001024013
  Tool = -> Fusion006002011004053036004001028003008
FEATURE [Part::Feature] Cut001024014001  label="Cut001024015"
  shape: bbox 77.5 x 57 x 14.5 mm, 30 faces (baked)
FEATURE [Part::Chamfer] Chamfer029006002
  Base = -> Cut001024014001
  Edges = 1 edges r=2: [Edge9]
FEATURE [Part::Feature] Fusion005
  Placement = pos=(7.5,-8.5,27) rot=(0,0,1;0rad)
  shape: bbox 30 x 30.99 x 10 mm, 24 faces, 3 solids (baked)
FEATURE [Part::Box] Box037  label="Cube037"
  AttacherType = Attacher::AttachEngine3D
  Height = 10
  Length = 14
  Placement = pos=(-6,-21.5,-10) rot=(0,0,1;0rad)
  Width = 43
FEATURE [Part::Fillet] Fillet003
  Base = -> Box037
  Edges = 2 edges r=1: [Edge1,Edge3]
FEATURE [Part::Cut] Cut001024014003  label="z-motor-plate-r2"
  Base = -> Cut001021
  Tool = -> Fillet003
FEATURE [Part::Refine] Cut001024014003001  label="z-motor-plate-r003"
  Source = -> Cut001024014003
FEATURE [Part::Feature] Cut001024014003001001  label="z-motor-plate-r004"
  shape: bbox 72.5 x 101 x 43 mm, 85 faces (baked)
FEATURE [Part::Box] Box038  label="Cube038"
  AttacherType = Attacher::AttachEngine3D
  Height = 5
  Length = 3
  Placement = pos=(45.5,23.5,20) rot=(0,0,1;0rad)
  Width = 6
FEATURE [Part::Cylinder] Cylinder039
  Angle = 360
  AttacherType = Attacher::AttachEngine3D
  Height = 3
  Placement = pos=(45.5,26.5,25) rot=(0,1,0;1.5708rad)
  Radius = 3
FEATURE [Part::MultiFuse] Fusion006002011004053036004001028003009
  Shapes = -> [Cylinder039,Box038]
FEATURE [Part::Feature] Cut001024014003001002001
  shape: bbox 77.5 x 57 x 14.5 mm, 87 faces (baked)
FEATURE [Part::Feature] Cut001003001  label="80-t-mellow"
  Placement = pos=(64.5,41,8.5) rot=(0,-1,0;1.5708rad)
  shape: bbox 18 x 55 x 55 mm, 10 faces (baked)
FEATURE [Part::Cylinder] Cylinder040
  Angle = 360
  AttacherType = Attacher::AttachEngine3D
  Height = 28
  Placement = pos=(40,41,8.5) rot=(0,1,0;1.5708rad)
  Radius = 19
FEATURE [Part::Cut] Cut001024014003001002002
  Base = -> Chamfer029006002
  Tool = -> Cylinder040
FEATURE [Part::Cut] Cut001024014003001002003
  Base = -> Cut001024014003001002002
  Tool = -> Fusion006002011004053036004001028003009
FEATURE [Part::Chamfer] Chamfer029006003
  Base = -> Cut001024014003001002003
  Edges = 2 edges r=0.4: [Edge27,Edge74]
FEATURE [Part::Feature] Cut001024014003001002005  label="z-motor-plate-r005"
  shape: bbox 72.5 x 101 x 43 mm, 85 faces (baked)
FEATURE [Part::Box] Box039  label="Cube039"
  AttacherType = Attacher::AttachEngine3D
  Height = 4.75
  Length = 24
  Placement = pos=(48.5,-26.5,30.25) rot=(0,0,1;0rad)
  Width = 47
FEATURE [Part::Chamfer] Chamfer029006004
  Base = -> Box039
  Edges = 2 edges r=1: [Edge5,Edge7]
FEATURE [Part::MultiFuse] Fusion006002011004053036004001028003010
  Shapes = -> [Chamfer029006004,Chamfer029006003,Fusion006002011004053036004001028003006]
FEATURE [Part::Cut] Cut001024014003001002006  label="cap-r1-f3"
  Base = -> Fusion006002011004053036004001028003010
  Tool = -> Fusion005
FEATURE [Part::Refine] Cut001024014003001002006001  label="cap-r1-f004"
  Source = -> Cut001024014003001002006
FEATURE [Part::Chamfer] Chamfer029006005
  Base = -> Cut001024014003001002006001
  Edges = 34 edges r=0.4: [Edge3,Edge5,Edge10,Edge51,Edge56,Edge62,Edge64,Edge76,Edge79,Edge83,Edge85,Edge87,Edge126,Edge129,Edge132,Edge134,Edge136,Edge138,Edge139,Edge141,Edge144,Edge146,Edge148,Edge150,Edge151,Edge152,Edge155,Edge158,Edge160,Edge162,Edge164,Edge165,Edge196,Edge197]
FEATURE [Part::Feature] Chamfer029006005001
  shape: bbox 99.5 x 57 x 14.5 mm, 102 faces (baked)
FEATURE [Part::Feature] _x_right_cover001001001_solid  label="_x_right_cover001001001 (Solid)"
  Placement = pos=(51.25,46.6,33) rot=(1,0,0;3.14159rad)
  shape: bbox 42.5 x 53.8 x 15 mm, 58 faces (baked)
FEATURE [Part::Box] Box040  label="Cube040"
  AttacherType = Attacher::AttachEngine3D
  Height = 4
  Length = 2
  Placement = pos=(70.5,22.5,27) rot=(0,0,1;0rad)
  Width = 37.3
FEATURE [Part::Chamfer] Chamfer029006005002
  Base = -> Box040
  Edges = 1 edges r=3: [Edge11]
FEATURE [Part::MultiFuse] Fusion006002011004053036004001028003011
  Shapes = -> [Chamfer029006005002,_x_right_cover001001001_solid]
FEATURE [Part::Refine] Fusion006002011004053036004001028003011001
  Source = -> Fusion006002011004053036004001028003011
FEATURE [Part::Feature] Fusion006002011004053036004001028003011001001
  shape: bbox 42.5 x 53.8 x 15 mm, 57 faces (baked)
